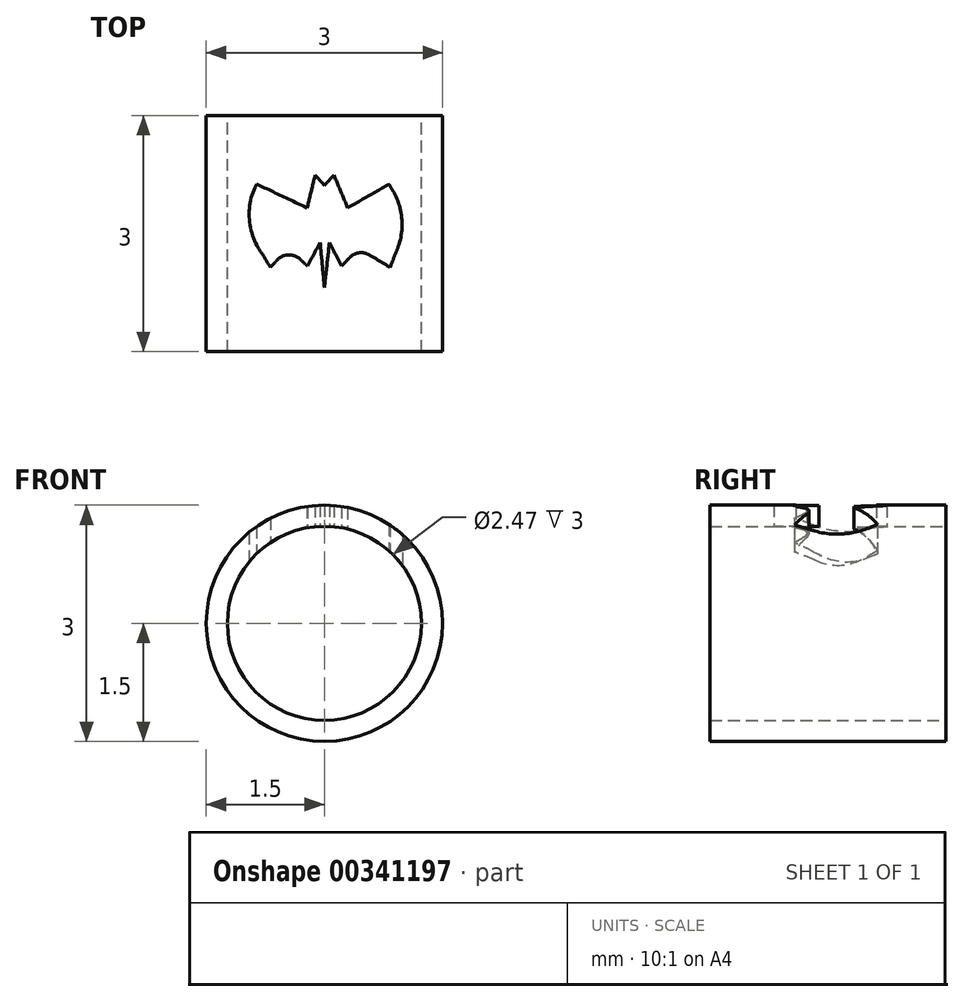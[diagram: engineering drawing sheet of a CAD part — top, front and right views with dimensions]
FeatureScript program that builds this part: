
annotation { "Feature Type Name" : "Feature", "Feature Type Description" : "" }
export const myFeature = defineFeature(function(context is Context, id is Id, definition is map)
    precondition{}
    {
        {
            var Q0;
            Q0=qCreatedBy(makeId("Front.planeOp"),FACE);
            var sketch = newSketch(context, id + "F0", { "sketchPlane" : qUnion([Q0])});
            skCircle(sketch, "E0", {"center": v(0, 0) * mm, "radius": 1.5 * mm});
            skCircle(sketch, "E1", {"center": v(0, 0) * mm, "radius": 1.23 * mm});
            skSolve(sketch);
        }
        {
            var Q0;
            Q0 = qSketchRegion(id + "F0", true);
            extrude(context, id + "F1", {"entities" : qUnion([Q0]), "depth" : 3 * mm});
        }
        {
            var Q0;
            Q0=qCreatedBy(makeId("Top.planeOp"),FACE);
            var sketch = newSketch(context, id + "F2", { "sketchPlane" : qUnion([Q0])});
            skLineSegment(sketch, "E2", {"start": v(-0.05, -1.61) * mm, "end": v(0, -2.19) * mm});
            skLineSegment(sketch, "E3", {"start": v(0, -2.19) * mm, "end": v(0.06, -1.61) * mm});
            skLineSegment(sketch, "E4", {"start": v(0.3, -1.17) * mm, "end": v(0.12, -0.76) * mm});
            skLineSegment(sketch, "E5", {"start": v(0.12, -0.76) * mm, "end": v(0, -0.89) * mm});
            skLineSegment(sketch, "E6", {"start": v(0, -0.89) * mm, "end": v(-0.12, -0.76) * mm});
            skLineSegment(sketch, "E7", {"start": v(-0.12, -0.76) * mm, "end": v(-0.22, -1.17) * mm});
            skLineSegment(sketch, "E8", {"start": v(-0.22, -1.17) * mm, "end": v(-0.86, -0.87) * mm});
            skLineSegment(sketch, "E9", {"start": v(0.82, -0.87) * mm, "end": v(0.3, -1.17) * mm});
            skLineSegment(sketch, "E10", {"start": v(0.82, -0.87) * mm, "end": v(0.88, -0.98) * mm});
            skLineSegment(sketch, "E11", {"start": v(0.94, -1.67) * mm, "end": v(0.84, -1.93) * mm});
            skLineSegment(sketch, "E12", {"start": v(-0.86, -0.87) * mm, "end": v(-0.88, -0.92) * mm});
            skLineSegment(sketch, "E13", {"start": v(-0.84, -1.68) * mm, "end": v(-0.69, -1.93) * mm});
            skArc(sketch, "E14.filletArc", {"start": v(-0.88, -0.92) * mm, "mid": v(-0.96, -1.3) * mm, "end": v(-0.84, -1.68) * mm});
            skArc(sketch, "E15.filletArc", {"start": v(0.94, -1.67) * mm, "mid": v(0.99, -1.32) * mm, "end": v(0.88, -0.98) * mm});
            skLineSegment(sketch, "E16", {"start": v(-0.69, -1.93) * mm, "end": v(-0.6, -1.83) * mm});
            skLineSegment(sketch, "E17", {"start": v(-0.31, -1.82) * mm, "end": v(-0.22, -1.91) * mm});
            skLineSegment(sketch, "E18", {"start": v(-0.22, -1.91) * mm, "end": v(-0.05, -1.61) * mm});
            skLineSegment(sketch, "E19", {"start": v(0.06, -1.61) * mm, "end": v(0.22, -1.91) * mm});
            skLineSegment(sketch, "E20", {"start": v(0.22, -1.91) * mm, "end": v(0.32, -1.8) * mm});
            skLineSegment(sketch, "E21", {"start": v(0.57, -1.77) * mm, "end": v(0.84, -1.93) * mm});
            skPoint(sketch, "E22.visualSharp", {"position": v(-0.46, -1.69) * mm});
            skArc(sketch, "E22.filletArc", {"start": v(-0.31, -1.82) * mm, "mid": v(-0.46, -1.77) * mm, "end": v(-0.6, -1.83) * mm});
            skPoint(sketch, "E23.visualSharp", {"position": v(0.43, -1.69) * mm});
            skArc(sketch, "E23.filletArc", {"start": v(0.57, -1.77) * mm, "mid": v(0.44, -1.74) * mm, "end": v(0.32, -1.8) * mm});
            skSolve(sketch);
        }
        {
            var Q0;
            Q0 = qSketchRegion(id + "F2", true);
            extrude(context, id + "F3", {"entities" : qUnion([Q0]), "operationType" : NewBodyOperationType.ADD, "depth" : 1.5 * mm});
        }
        {
            var Q0;
            Q0=makeQuery(id+"F3.opExtrude","CAP_FACE",FACE,{"disambiguationData":[OSD([sQuery(id+"F2.wireOp",EDGE,"HBpyUWsg-iOUA-USBf-g4An-A8PF0lOxMa5W"),sQuery(id+"F2.wireOp",EDGE,"YCUSnPi1-6mBL-k2ud-Um4Z-XTyq9TVPgLlK"),sQuery(id+"F2.wireOp",EDGE,"Fy7eg5A6-INUC-jNbn-nhOz-cuvrAxA0WHgH"),sQuery(id+"F2.wireOp",EDGE,"WssaEOCH-7eNh-v4Nc-tKoS-16i0Iyfqz10y"),sQuery(id+"F2.wireOp",EDGE,"AoGTwEJK-SYZX-l9nZ-DJrV-EVHcphp3kmZh"),sQuery(id+"F2.wireOp",EDGE,"E2"),sQuery(id+"F2.wireOp",EDGE,"E3"),sQuery(id+"F2.wireOp",EDGE,"vJqWgjbj-qyaU-7jg5-LK7F-qgsnqq65Wd4p"),sQuery(id+"F2.wireOp",EDGE,"g7MHFEKV-5hNa-oiVU-gNKN-G57xu9rIisnM"),sQuery(id+"F2.wireOp",EDGE,"Um21zWyf-tQk8-Zjvt-xZf5-ILJV0nye34Hc"),sQuery(id+"F2.wireOp",EDGE,"ayJXg8lA-QMA1-JIVQ-dAOV-FvHFggYPNhku"),sQuery(id+"F2.wireOp",EDGE,"E4"),sQuery(id+"F2.wireOp",EDGE,"E5"),sQuery(id+"F2.wireOp",EDGE,"E6"),sQuery(id+"F2.wireOp",EDGE,"E7"),sQuery(id+"F2.wireOp",EDGE,"E8"),sQuery(id+"F2.wireOp",EDGE,"5EJCx7Cs-oHhz-3jQz-In0x-56L6zh3ZaaU6"),sQuery(id+"F2.wireOp",EDGE,"E9")])],"isStart":true});
            extrude(context, id + "F4", {"entities" : qUnion([Q0]), "operationType" : NewBodyOperationType.REMOVE, "oppositeDirection" : true, "depth" : 25 * mm});
        }
    });
